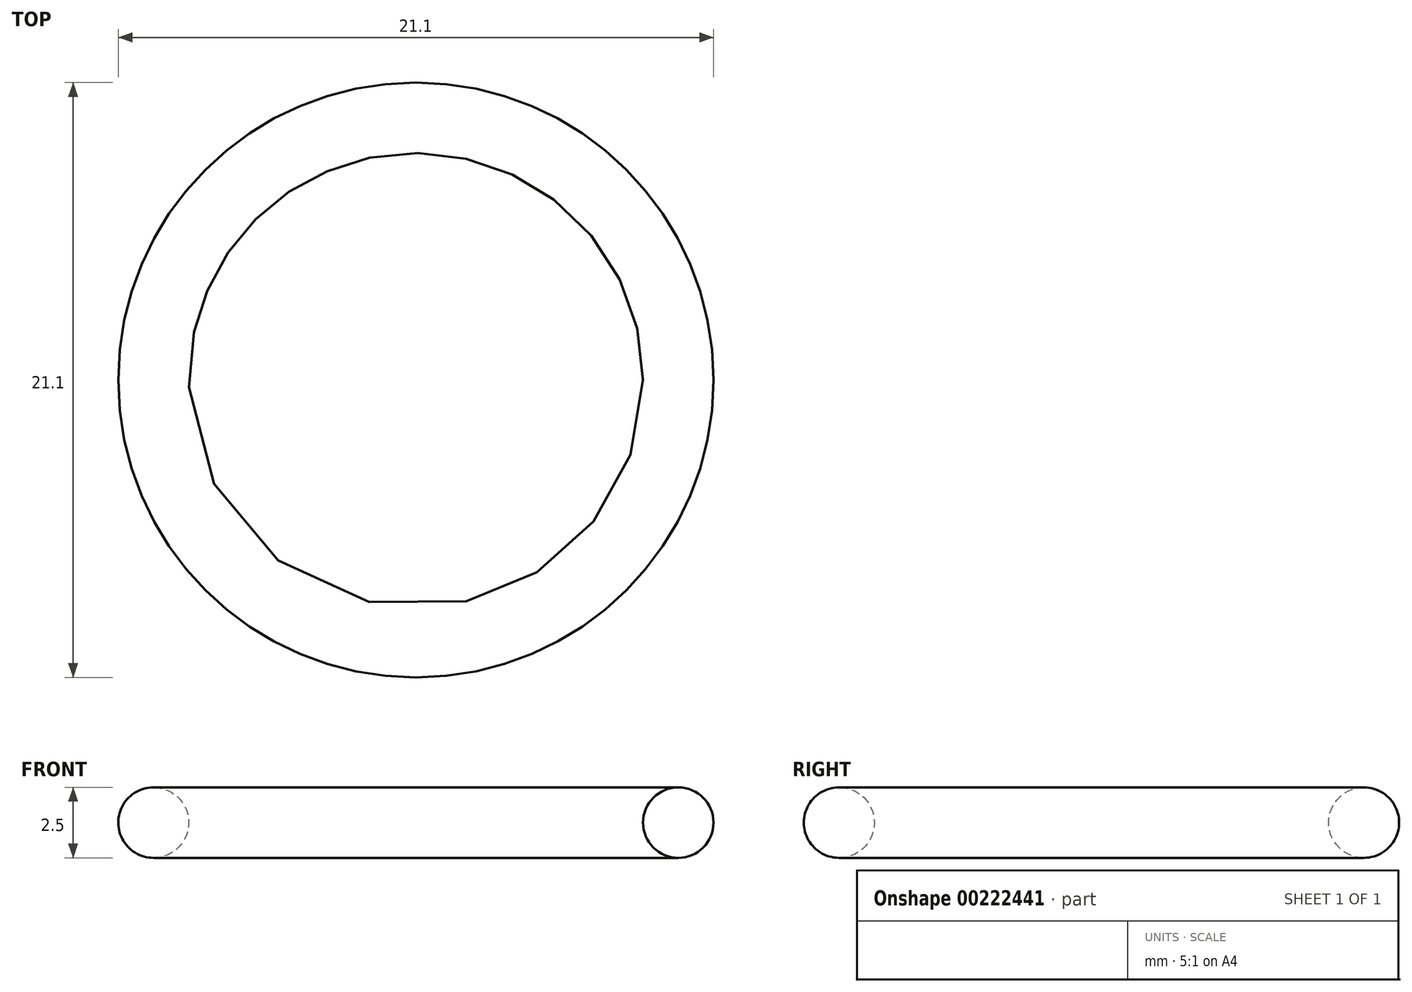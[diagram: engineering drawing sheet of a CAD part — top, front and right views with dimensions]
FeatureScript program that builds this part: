
annotation { "Feature Type Name" : "Feature", "Feature Type Description" : "" }
export const myFeature = defineFeature(function(context is Context, id is Id, definition is map)
    precondition{}
    {
        {
            var Q0;
            Q0=qCreatedBy(makeId("Front.planeOp"),FACE);
            var sketch = newSketch(context, id + "F0", { "sketchPlane" : qUnion([Q0])});
            skCircle(sketch, "E0", {"center": v(-9.3, 1.85) * mm, "radius": 1.25 * mm});
            skLineSegment(sketch, "E1", {"start": v(0, 12.58) * mm, "end": v(0, -11.43) * mm, "construction": true});
            skSolve(sketch);
        }
        {
            var Q0;
            Q0=makeQuery(id+"F0.imprint","IMPRINT",FACE,{"disambiguationData":[TD([[makeQuery(id+"F0.imprint","IMPRINT",EDGE,{"derivedFrom":sQuery(id+"F0.wireOp",EDGE,"E0")}),1.0]])]});
            var Q1;
            Q1=sQuery(id+"F0.wireOp",EDGE,"E1");
            revolve(context, id + "F1", {"entities" : qUnion([Q0]), "axis" : qUnion([Q1]), "revolveType" : RevolveType.FULL});
        }
    });
